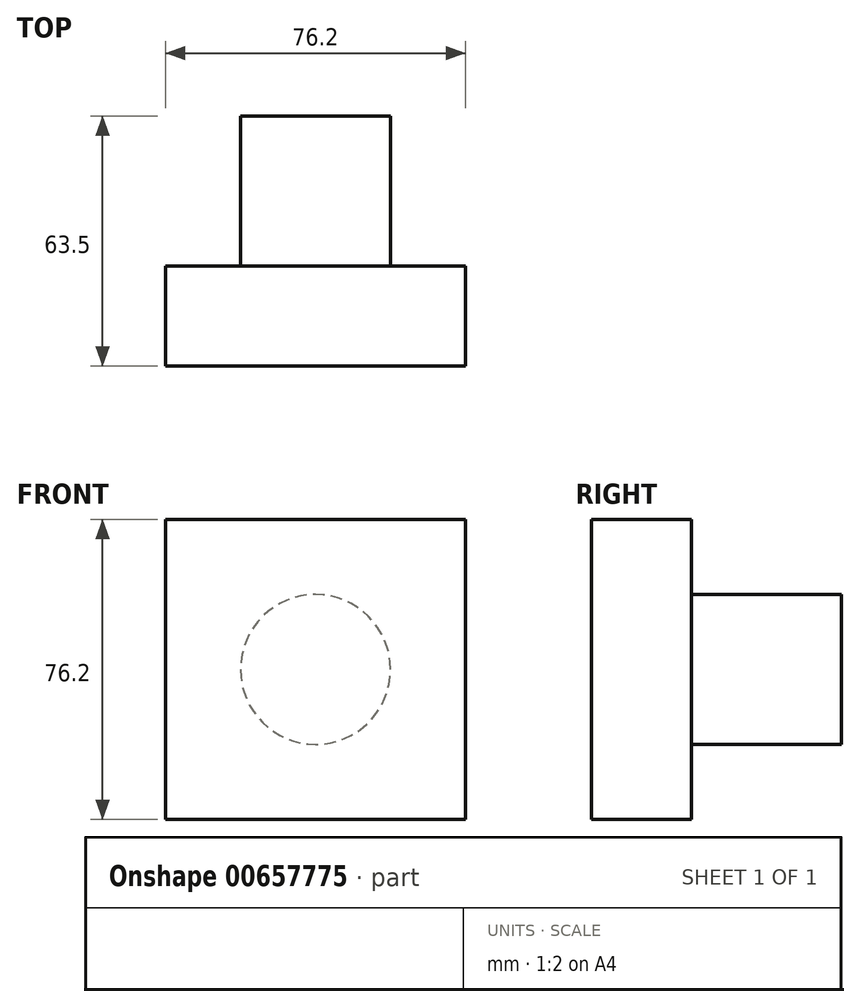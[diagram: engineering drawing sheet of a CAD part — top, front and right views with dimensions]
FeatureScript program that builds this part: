
annotation { "Feature Type Name" : "Feature", "Feature Type Description" : "" }
export const myFeature = defineFeature(function(context is Context, id is Id, definition is map)
    precondition{}
    {
        {
            var Q0;
            Q0=qCreatedBy(makeId("Front.planeOp"),FACE);
            var sketch = newSketch(context, id + "F0", { "sketchPlane" : qUnion([Q0])});
            skLineSegment(sketch, "E0.bottom", {"start": v(-38.1, 38.1) * mm, "end": v(38.1, 38.1) * mm});
            skLineSegment(sketch, "E0.top", {"start": v(-38.1, -38.1) * mm, "end": v(38.1, -38.1) * mm});
            skLineSegment(sketch, "E0.left", {"start": v(-38.1, 38.1) * mm, "end": v(-38.1, -38.1) * mm});
            skLineSegment(sketch, "E0.right", {"start": v(38.1, 38.1) * mm, "end": v(38.1, -38.1) * mm});
            skPoint(sketch, "E0.middle", {"position": v(0, 0) * mm});
            skSolve(sketch);
        }
        {
            var Q0;
            Q0=makeQuery(id+"F0.imprint","IMPRINT",FACE,{"disambiguationData":[TD([[makeQuery(id+"F0.imprint","IMPRINT",EDGE,{"derivedFrom":sQuery(id+"F0.wireOp",EDGE,"E0.bottom")}),-1.0]])]});
            var sketch = newSketch(context, id + "F1", { "sketchPlane" : qUnion([Q0])});
            skCircle(sketch, "E1", {"center": v(0, 0) * mm, "radius": 19.05 * mm});
            skSolve(sketch);
        }
        {
            var Q0;
            Q0=makeQuery(id+"F0.imprint","IMPRINT",FACE,{"disambiguationData":[TD([[makeQuery(id+"F0.imprint","IMPRINT",EDGE,{"derivedFrom":sQuery(id+"F0.wireOp",EDGE,"E0.bottom")}),-1.0]])]});
            extrude(context, id + "F2", {"entities" : qUnion([Q0]), "depth" : 25.4 * mm, "offsetDistance" : 25.4 * mm});
        }
        {
            var Q0;
            Q0=makeQuery(id+"F1.imprint","IMPRINT",FACE,{"disambiguationData":[TD([[makeQuery(id+"F1.imprint","IMPRINT",EDGE,{"derivedFrom":sQuery(id+"F1.wireOp",EDGE,"E1")}),1.0]])]});
            extrude(context, id + "F3", {"entities" : qUnion([Q0]), "operationType" : NewBodyOperationType.ADD, "oppositeDirection" : true, "depth" : 38.1 * mm, "offsetDistance" : 25.4 * mm});
        }
    });
